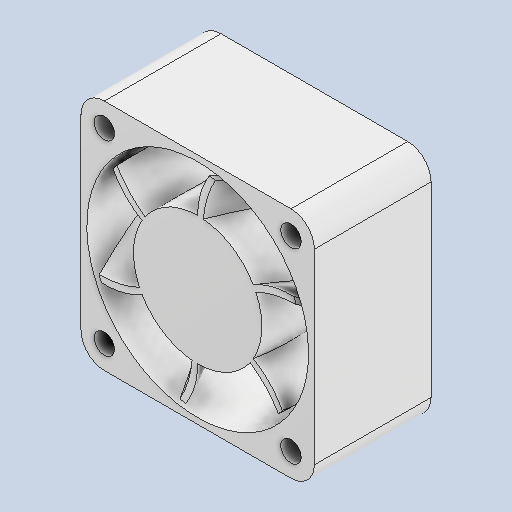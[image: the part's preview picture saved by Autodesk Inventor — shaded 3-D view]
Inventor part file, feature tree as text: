
AUTODESK INVENTOR PART (.ipt)
format: ipt  version: 2022 (Build 260153070, 153G)  size: 336,384 bytes
history: native  units: in
note: dims shown in document units (in); Inventor stores cm internally (conversion verified against a paired STEP export)
features: sketch x5, extrude x3, fillet x1, plane x1, loft x1, pattern_circular x1
ambient origin geometry x8: Origin, YZ Plane, XZ Plane, XY Plane, X Axis, Y Axis, Z Axis, Center Point
bodies: Solid1 (feature_tree)
feature tree (12):
  extrude  "Extrusion1"  Depth=1.2598in
  extrude  "Extrusion2"  Depth=0.1378in
  fillet  "Fillet1"  Radius=0.1378in
  sketch  "Sketch3"  dims[d7=0.1378in d8=1.4961in d9=0.7874in d10=0.0in]
  plane  "Work Plane1"
  loft  "Loft2"
  pattern_circular  "Circular Pattern1"  Count=2  [1 undecoded]
  extrude  "Extrusion3"  Depth=0.7087in TaperAngle=0.0deg
  sketch  "Sketch1"  dims[d0=1.5748in d3=1.2598in]
  sketch  "Sketch2"  dims[d4=0.1378in d5=0.1378in d6=0.1378in]
  sketch  "Sketch4"  dims[d11=0.8661in d12=0.7087in d13=0.0in]
  sketch  "Sketch5"  dims[d14=0.0787in d15=1.4961in d17=0.0344in d19=0.055in d20=-0.6299in d21=0.0344in d23=0.055in d24=30.0deg d29=0.0in d30=90.0deg d31=0.0in d32=90.0deg d33=2.3622in d34=360.0deg d36=0.0394in d37=0.7087in d38=0.0in]
note: 1 required parameter value undecoded (feature->parameter linkage not recoverable at this tier; creation-order binding heuristic only, values carry confidence <= 0.55)
